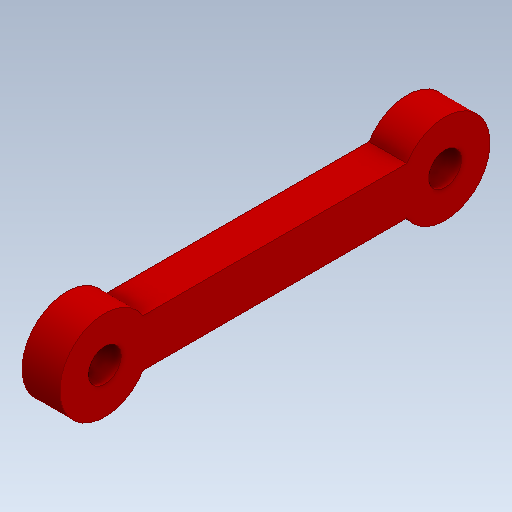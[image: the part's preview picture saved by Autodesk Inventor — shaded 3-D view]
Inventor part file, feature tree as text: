
AUTODESK INVENTOR PART (.ipt)
format: ipt  version: 2020 (Build 240168000, 168)  size: 125,440 bytes
history: native  units: in
note: dims shown in document units (in); Inventor stores cm internally (conversion verified against a paired STEP export)
features: extrude x1, sketch x1
ambient origin geometry x8: Origin, YZ Plane, XZ Plane, XY Plane, X Axis, Y Axis, Z Axis, Center Point
bodies: Solid1 (feature_tree)
feature tree (2):
  extrude  "Extrusion1"  Depth=1.4173in
  sketch  "Sketch1"  dims[d0=0.1378in d1=1.4173in d2=0.1181in d3=0.1181in d4=0.1969in d5=0.1575in d6=0.0in]
